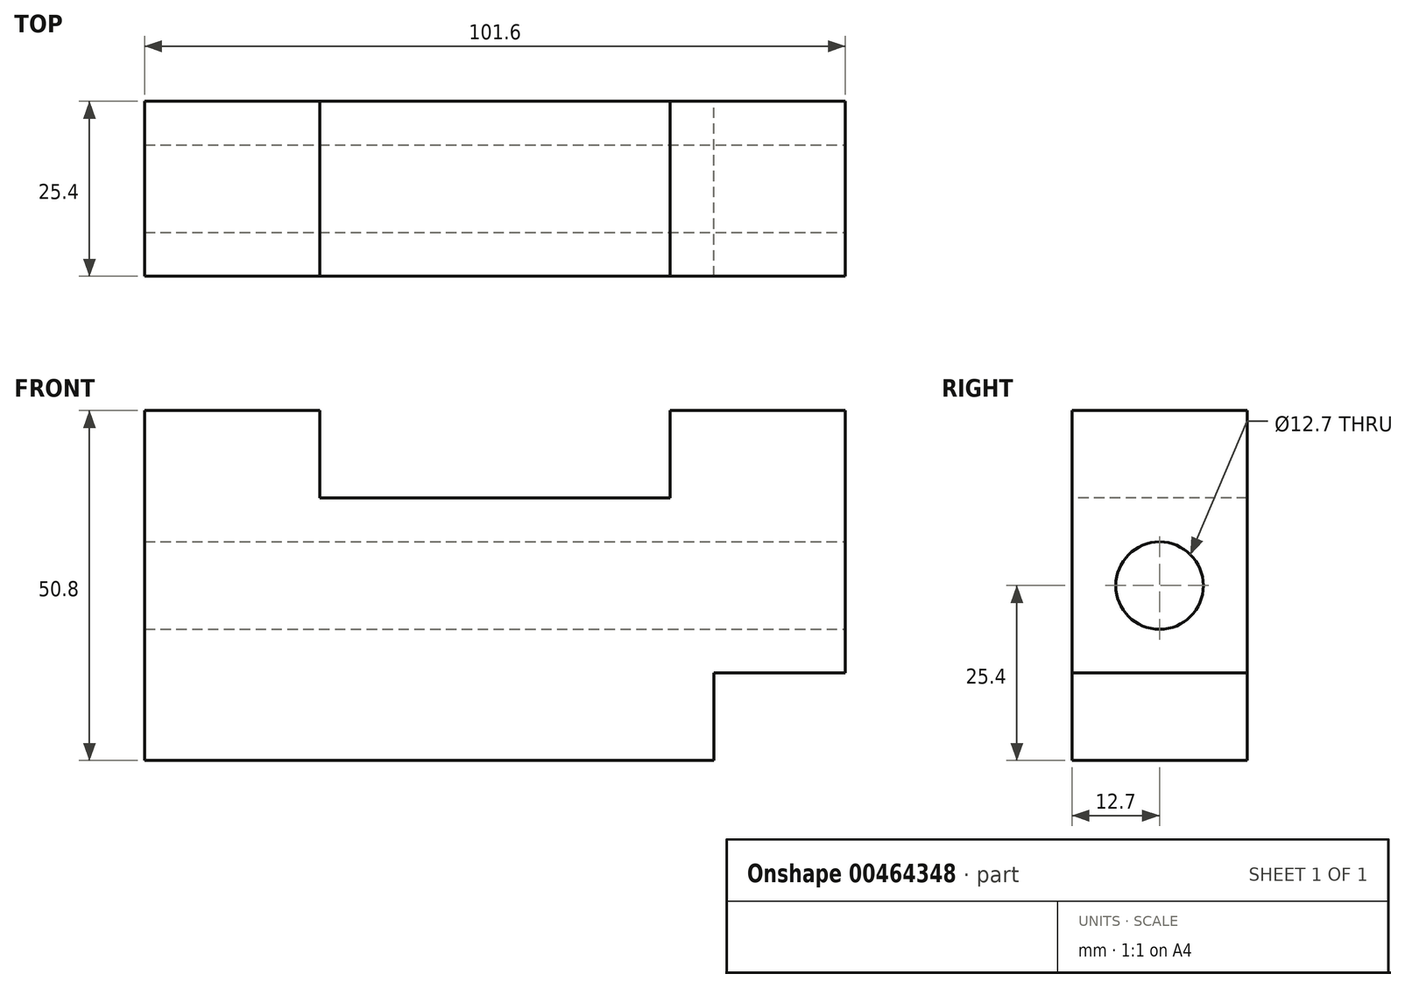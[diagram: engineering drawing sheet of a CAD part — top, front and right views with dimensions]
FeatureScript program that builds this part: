
annotation { "Feature Type Name" : "Feature", "Feature Type Description" : "" }
export const myFeature = defineFeature(function(context is Context, id is Id, definition is map)
    precondition{}
    {
        {
            var Q0;
            Q0=qCreatedBy(makeId("Front.planeOp"),FACE);
            var sketch = newSketch(context, id + "F0", { "sketchPlane" : qUnion([Q0])});
            skLineSegment(sketch, "E0.bottom", {"start": v(50.8, 25.4) * mm, "end": v(-50.8, 25.4) * mm});
            skLineSegment(sketch, "E0.top", {"start": v(50.8, -25.4) * mm, "end": v(-50.8, -25.4) * mm});
            skLineSegment(sketch, "E0.left", {"start": v(50.8, 25.4) * mm, "end": v(50.8, -25.4) * mm});
            skLineSegment(sketch, "E0.right", {"start": v(-50.8, 25.4) * mm, "end": v(-50.8, -25.4) * mm});
            skPoint(sketch, "E0.middle", {"position": v(0, 0) * mm});
            skSolve(sketch);
        }
        {
            var Q0;
            Q0=makeQuery(id+"F0.imprint","IMPRINT",FACE,{"disambiguationData":[TD([[makeQuery(id+"F0.imprint","IMPRINT",EDGE,{"derivedFrom":sQuery(id+"F0.wireOp",EDGE,"E0.bottom")}),1.0]])]});
            extrude(context, id + "F1", {"entities" : qUnion([Q0]), "depth" : 25.4 * mm});
        }
        {
            var Q0;
            Q0=makeQuery(id+"F1.opExtrude","SWEPT_FACE",FACE,{"disambiguationData":[OSD([sQuery(id+"F0.wireOp",EDGE,"E0.left")])]});
            var sketch = newSketch(context, id + "F2", { "sketchPlane" : qUnion([Q0])});
            skCircle(sketch, "E1", {"center": v(-12.7, 0) * mm, "radius": 6.35 * mm});
            skSolve(sketch);
        }
        {
            var Q0;
            Q0=makeQuery(id+"F2.imprint","IMPRINT",FACE,{"disambiguationData":[TD([[makeQuery(id+"F2.imprint","IMPRINT",EDGE,{"derivedFrom":sQuery(id+"F2.wireOp",EDGE,"E1")}),1.0]])]});
            extrude(context, id + "F3", {"entities" : qUnion([Q0]), "operationType" : NewBodyOperationType.REMOVE, "endBound" : BoundingType.THROUGH_ALL, "oppositeDirection" : true, "depth" : 25.4 * mm});
        }
        {
            var Q0;
            Q0=makeQuery(id+"F1.opExtrude","SWEPT_FACE",FACE,{"disambiguationData":[OSD([sQuery(id+"F0.wireOp",EDGE,"E0.left")])]});
            var sketch = newSketch(context, id + "F4", { "sketchPlane" : qUnion([Q0])});
            skLineSegment(sketch, "E2", {"start": v(0, -12.7) * mm, "end": v(-25.4, -12.7) * mm});
            skLineSegment(sketch, "E3.top", {"start": v(-25.4, -25.4) * mm, "end": v(0, -25.4) * mm});
            skLineSegment(sketch, "E3.left", {"start": v(-25.4, -12.7) * mm, "end": v(-25.4, -25.4) * mm});
            skLineSegment(sketch, "E3.right", {"start": v(0, -12.7) * mm, "end": v(0, -25.4) * mm});
            skSolve(sketch);
        }
        {
            var Q0;
            Q0=makeQuery(id+"F4.imprint","IMPRINT",FACE,{"disambiguationData":[TD([[makeQuery(id+"F4.imprint","IMPRINT",EDGE,{"derivedFrom":sQuery(id+"F4.wireOp",EDGE,"E2")}),1.0]])]});
            extrude(context, id + "F5", {"entities" : qUnion([Q0]), "operationType" : NewBodyOperationType.REMOVE, "oppositeDirection" : true, "depth" : 19.05 * mm});
        }
        {
            var Q0;
            Q0=makeQuery(id+"F1.opExtrude","CAP_FACE",FACE,{"disambiguationData":[OSD([sQuery(id+"F0.wireOp",EDGE,"E0.bottom"),sQuery(id+"F0.wireOp",EDGE,"E0.top"),sQuery(id+"F0.wireOp",EDGE,"E0.left"),sQuery(id+"F0.wireOp",EDGE,"E0.right")])],"isStart":false});
            var sketch = newSketch(context, id + "F6", { "sketchPlane" : qUnion([Q0])});
            skLineSegment(sketch, "E4.bottom", {"start": v(-25.4, 25.4) * mm, "end": v(25.4, 25.4) * mm});
            skLineSegment(sketch, "E4.top", {"start": v(-25.4, 12.7) * mm, "end": v(25.4, 12.7) * mm});
            skLineSegment(sketch, "E4.left", {"start": v(-25.4, 25.4) * mm, "end": v(-25.4, 12.7) * mm});
            skLineSegment(sketch, "E4.right", {"start": v(25.4, 25.4) * mm, "end": v(25.4, 12.7) * mm});
            skSolve(sketch);
        }
        {
            var Q0;
            Q0 = qSketchRegion(id + "F6", true);
            extrude(context, id + "F7", {"entities" : qUnion([Q0]), "operationType" : NewBodyOperationType.REMOVE, "endBound" : BoundingType.THROUGH_ALL, "oppositeDirection" : true, "depth" : 25.4 * mm});
        }
    });
